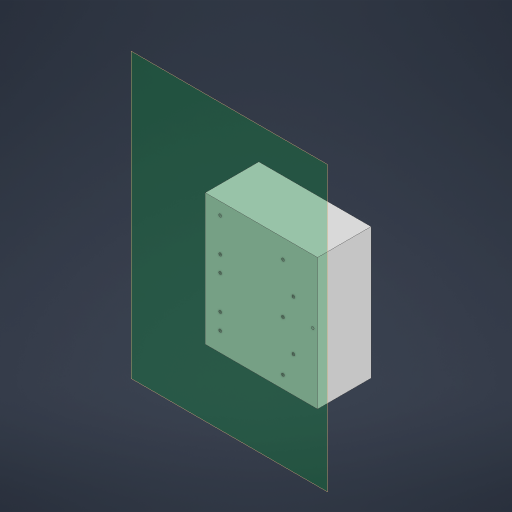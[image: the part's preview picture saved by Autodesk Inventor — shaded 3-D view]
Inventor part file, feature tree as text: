
AUTODESK INVENTOR PART (.ipt)
format: ipt  version: 2024.2 (Build 282272000, 272)  size: 515,072 bytes
history: native  units: in
note: dims shown in document units (in); Inventor stores cm internally (conversion verified against a paired STEP export)
features: other x3, sketch x2, plane x1, extrude x1, hole x1
ambient origin geometry x8: Origin, YZ Plane, XZ Plane, XY Plane, X Axis, Y Axis, Z Axis, Center Point
bodies: Solid2 (feature_tree), Solid1 (feature_tree)
feature tree (8):
  other  "HV servo drive v1_PCB.ipt"
  sketch  "Sketch1"  dims[d0=0.3937in d1=3.42in]
  plane  "Work Plane1"
  extrude  "Extrusion1"  Depth=3.42in
  hole  "Hole1"  [1 undecoded]
  other  "Solid1::HV servo drive v1_PCB.ipt"
  other  "TaggingFeature1"
  sketch  "Sketch2"  dims[d2=4.0in d3=3.47in d4=0.02in d5=0.25in d6=1.63in d7=0.0in d8=0.0849in d9=0.224in d10=0.119in d11=0.25in d12=0.5635in d13=0.28in d14=0.8108in]
note: 1 required parameter value undecoded (feature->parameter linkage not recoverable at this tier; creation-order binding heuristic only, values carry confidence <= 0.55)
